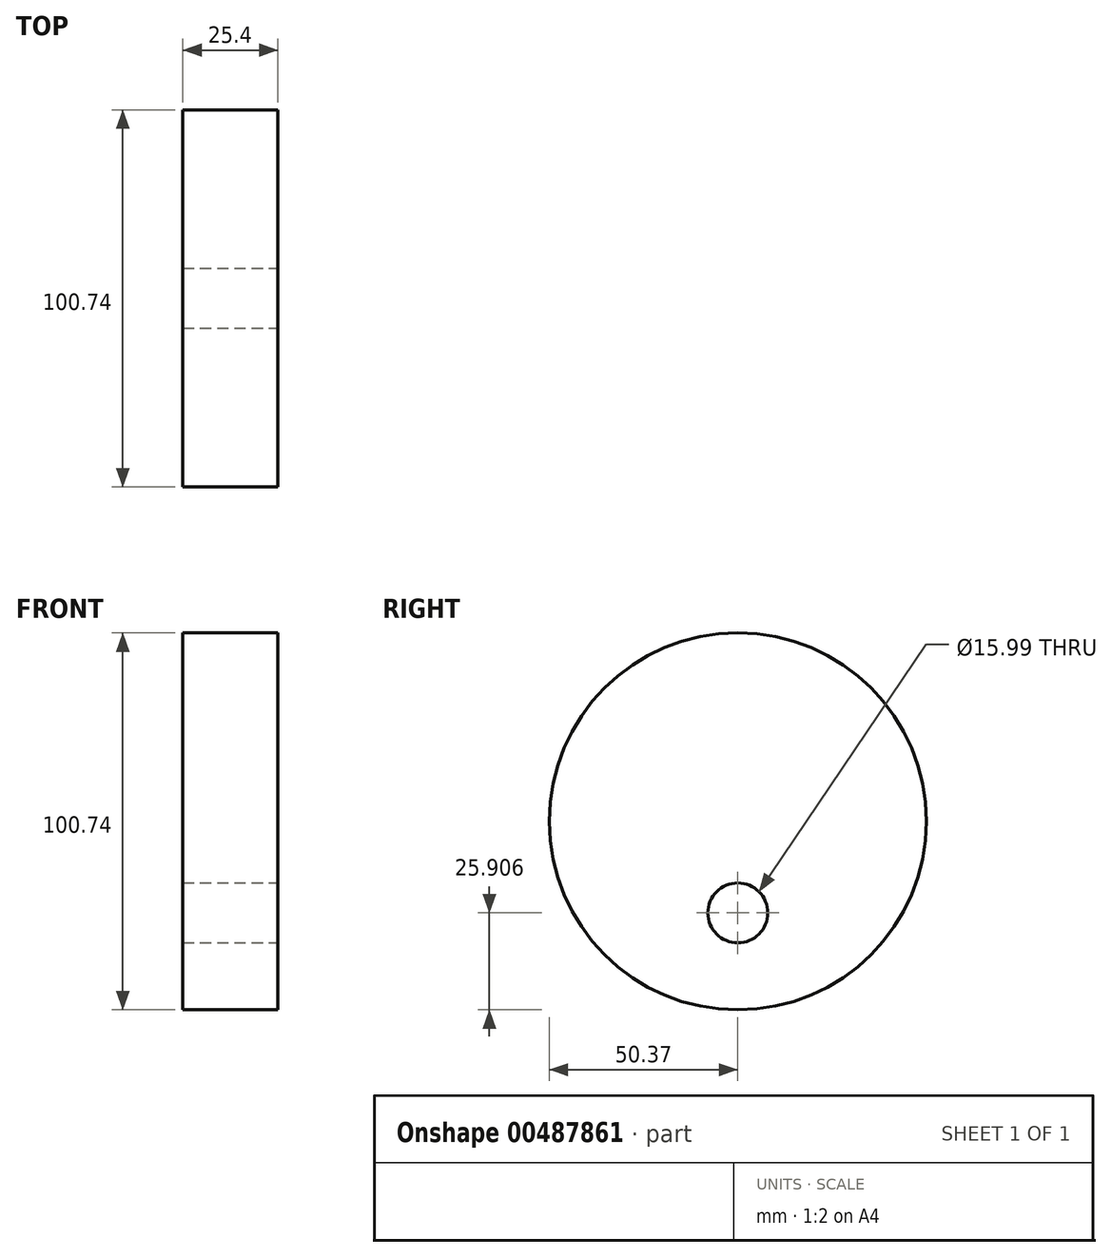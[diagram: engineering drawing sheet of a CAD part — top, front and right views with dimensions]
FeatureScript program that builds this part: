
annotation { "Feature Type Name" : "Feature", "Feature Type Description" : "" }
export const myFeature = defineFeature(function(context is Context, id is Id, definition is map)
    precondition{}
    {
        {
            var Q0;
            Q0=qCreatedBy(makeId("Right.planeOp"),FACE);
            var sketch = newSketch(context, id + "F0", { "sketchPlane" : qUnion([Q0])});
            skCircle(sketch, "E0", {"center": v(0, 0) * mm, "radius": 50.37 * mm});
            skSolve(sketch);
        }
        {
            var Q0;
            Q0 = qSketchRegion(id + "F0", true);
            extrude(context, id + "F1", {"entities" : qUnion([Q0]), "depth" : 25.4 * mm});
        }
        {
            var Q0;
            Q0=makeQuery(id+"F1.opExtrude","CAP_FACE",FACE,{"disambiguationData":[OSD([sQuery(id+"F0.wireOp",EDGE,"E0")])],"isStart":false});
            var sketch = newSketch(context, id + "F2", { "sketchPlane" : qUnion([Q0])});
            skCircle(sketch, "E1", {"center": v(0, -24.46) * mm, "radius": 8 * mm});
            skSolve(sketch);
        }
        {
            var Q0;
            Q0=makeQuery(id+"F2.imprint","IMPRINT",FACE,{"disambiguationData":[TD([[makeQuery(id+"F2.imprint","IMPRINT",EDGE,{"derivedFrom":sQuery(id+"F2.wireOp",EDGE,"E1")}),1.0]])]});
            extrude(context, id + "F3", {"entities" : qUnion([Q0]), "operationType" : NewBodyOperationType.REMOVE, "oppositeDirection" : true, "depth" : 25.4 * mm});
        }
        {
            var Q0;
            Q0=qCreatedBy(makeId("Right.planeOp"),FACE);
            var sketch = newSketch(context, id + "F4", { "sketchPlane" : qUnion([Q0])});
            skCircle(sketch, "E2", {"center": v(0, 0) * mm, "radius": 25.58 * mm});
            skSolve(sketch);
        }
    });
